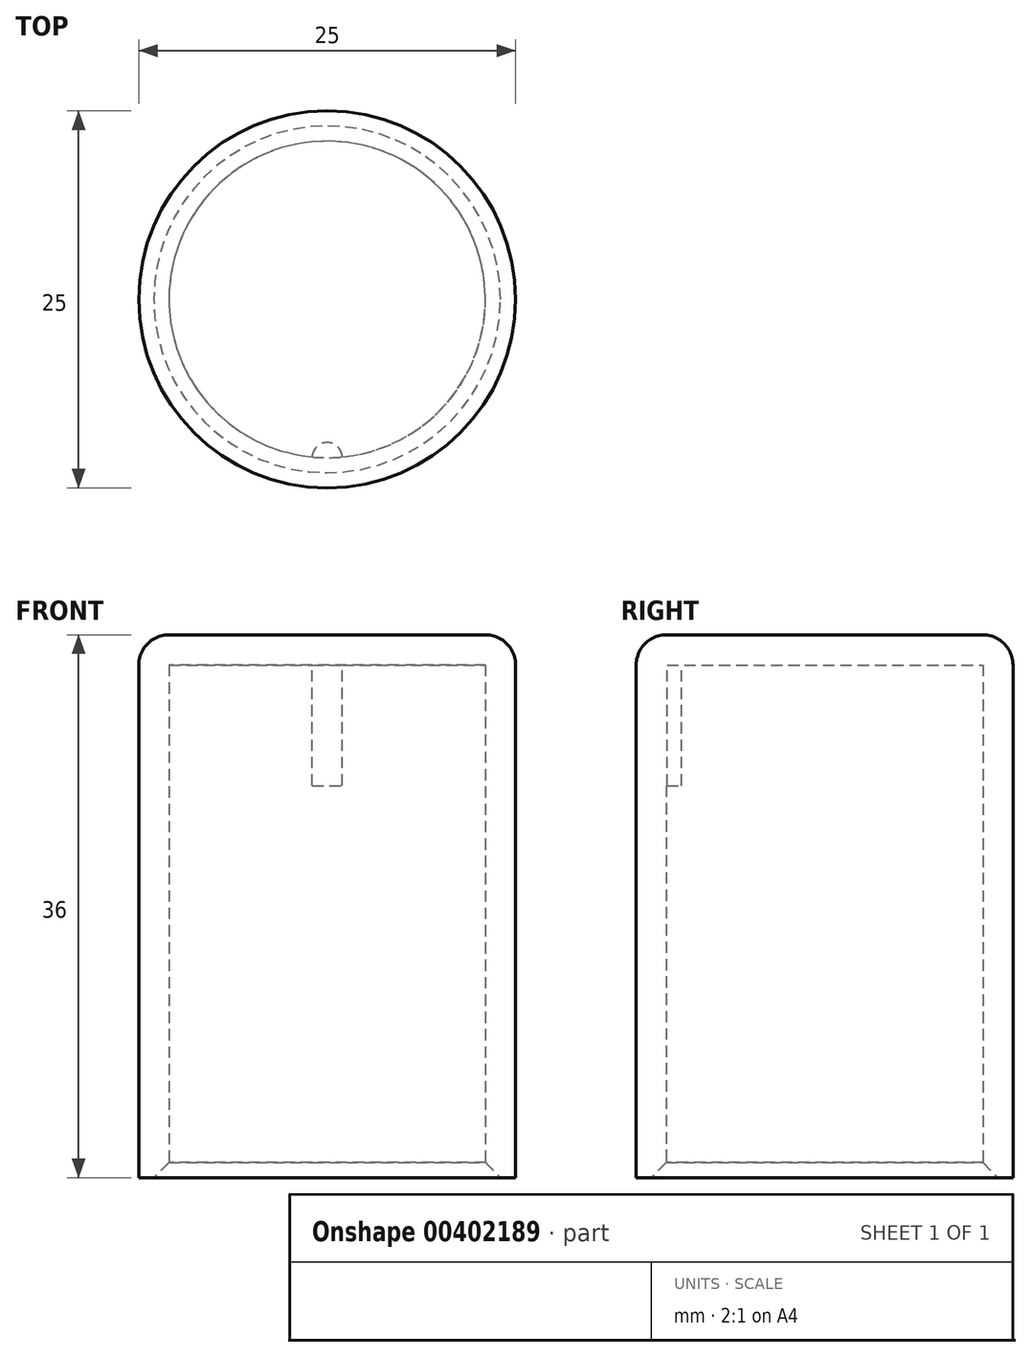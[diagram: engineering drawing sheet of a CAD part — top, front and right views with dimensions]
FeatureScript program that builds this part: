
annotation { "Feature Type Name" : "Feature", "Feature Type Description" : "" }
export const myFeature = defineFeature(function(context is Context, id is Id, definition is map)
    precondition{}
    {
        {
            var Q0;
            Q0=qCreatedBy(makeId("Top.planeOp"),FACE);
            var sketch = newSketch(context, id + "F0", { "sketchPlane" : qUnion([Q0])});
            skCircle(sketch, "E0", {"center": v(0, 0) * mm, "radius": 12.5 * mm});
            skSolve(sketch);
        }
        {
            var Q0;
            Q0 = qSketchRegion(id + "F0", true);
            extrude(context, id + "F1", {"entities" : qUnion([Q0]), "depth" : 36 * mm});
        }
        {
            var Q0;
            Q0=makeQuery(id+"F1.opExtrude","CAP_EDGE",EDGE,{"disambiguationData":[OSD([sQuery(id+"F0.wireOp",EDGE,"E0")])],"isStart":false});
            fillet(context, id + "F2", {"entities" : qUnion([Q0]), "radius" : 2 * mm, "tangentPropagation" : true, "allowEdgeOverflow" : false});
        }
        {
            var Q0;
            Q0=makeQuery(id+"F1.opExtrude","CAP_FACE",FACE,{"disambiguationData":[OSD([sQuery(id+"F0.wireOp",EDGE,"E0")])],"isStart":true});
            shell(context, id + "F3", {"entities" : qUnion([Q0]), "thickness" : 2 * mm});
        }
        {
            var Q0;
            {var subQ0=sQuery(id+"F0.wireOp",EDGE,"E0");Q0=makeQuery(id+"F3.opShell","OFFSET_EDGE",EDGE,{"disambiguationData":[OSD([subQ0]),TDD([makeQuery(id+"F1.opExtrude","CAP_EDGE",EDGE,{"disambiguationData":[OSD([subQ0])],"isStart":true})])]});}
            chamfer(context, id + "F4", {"entities" : qUnion([Q0]), "width" : 1 * mm, "tangentPropagation" : true});
        }
        {
            var Q0;
            {var subQ0=sQuery(id+"F0.wireOp",EDGE,"E0");Q0=makeQuery(id+"F3.opShell","OFFSET_FACE",FACE,{"disambiguationData":[OSD([subQ0]),TDD([makeQuery(id+"F1.opExtrude","CAP_FACE",FACE,{"disambiguationData":[OSD([subQ0])],"isStart":false})])]});}
            var sketch = newSketch(context, id + "F5", { "sketchPlane" : qUnion([Q0])});
            skArc(sketch, "E1", {"start": v(1, 10.45) * mm, "mid": v(0, 10.5) * mm, "end": v(-1, 10.45) * mm});
            skArc(sketch, "E2", {"start": v(-1, 10.45) * mm, "mid": v(0, 9.5) * mm, "end": v(1, 10.45) * mm});
            skSolve(sketch);
        }
        {
            var Q0;
            Q0 = qSketchRegion(id + "F5", true);
            extrude(context, id + "F6", {"entities" : qUnion([Q0]), "operationType" : NewBodyOperationType.ADD, "depth" : 8 * mm});
        }
    });
